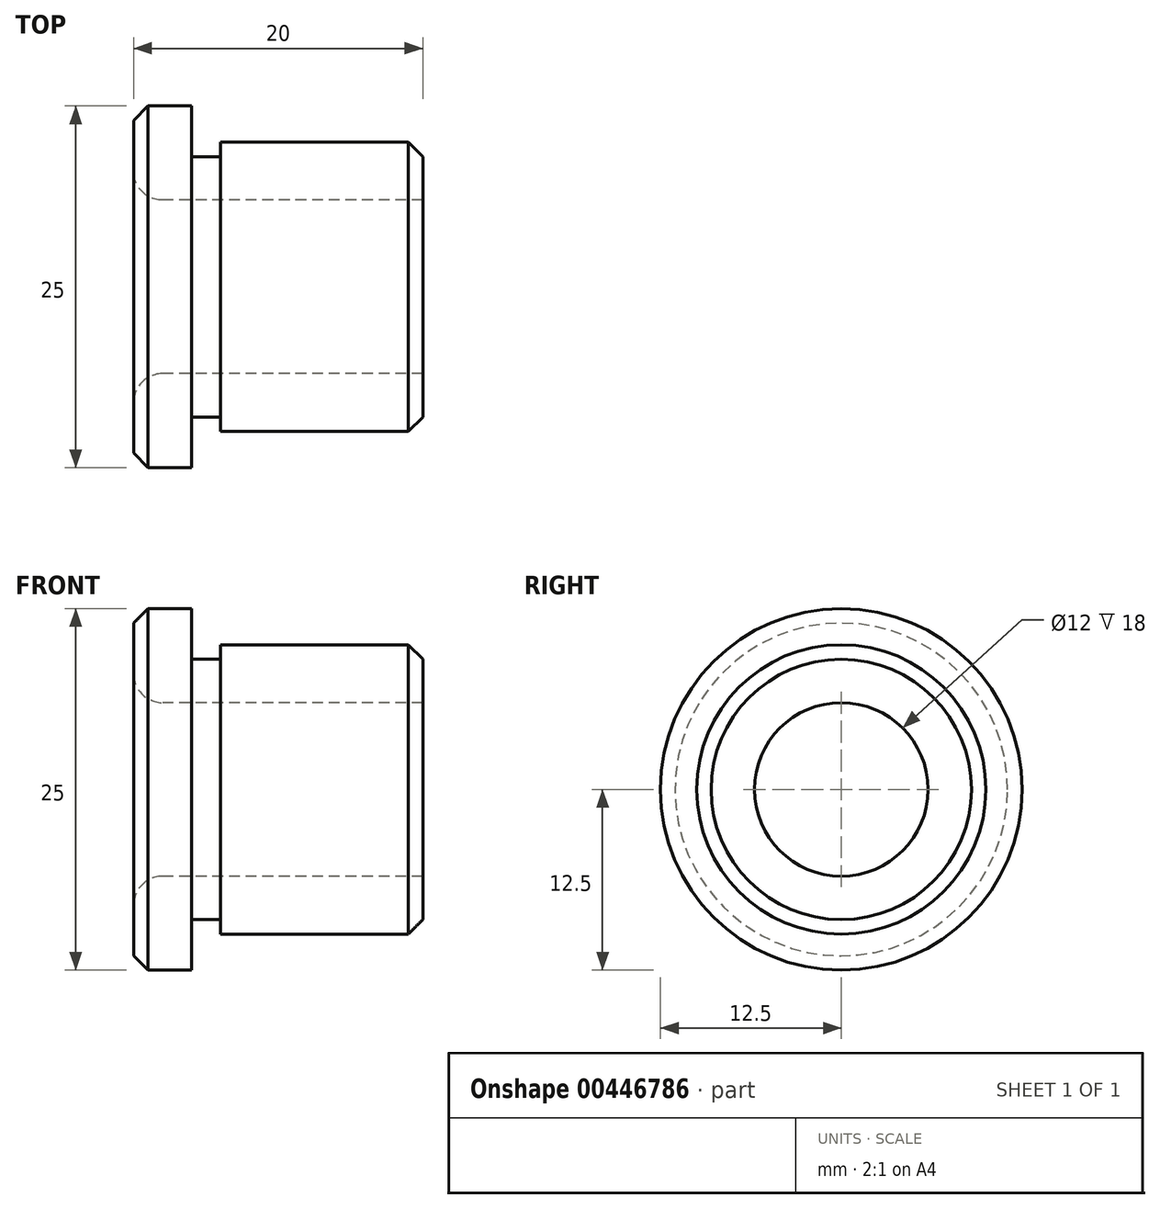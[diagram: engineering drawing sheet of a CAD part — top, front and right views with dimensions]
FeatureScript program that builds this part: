
annotation { "Feature Type Name" : "Feature", "Feature Type Description" : "" }
export const myFeature = defineFeature(function(context is Context, id is Id, definition is map)
    precondition{}
    {
        {
            var Q0;
            Q0=qCreatedBy(makeId("Front.planeOp"),FACE);
            var sketch = newSketch(context, id + "F0", { "sketchPlane" : qUnion([Q0])});
            skLineSegment(sketch, "E0", {"start": v(0, 0) * mm, "end": v(25.35, 0) * mm, "construction": true});
            skLineSegment(sketch, "E1", {"start": v(0, 8) * mm, "end": v(0, 12.5) * mm});
            skLineSegment(sketch, "E2", {"start": v(0, 12.5) * mm, "end": v(4, 12.5) * mm});
            skLineSegment(sketch, "E3", {"start": v(4, 12.5) * mm, "end": v(4, 9) * mm});
            skLineSegment(sketch, "E4", {"start": v(4, 9) * mm, "end": v(6, 9) * mm});
            skLineSegment(sketch, "E5", {"start": v(6, 9) * mm, "end": v(6, 10) * mm});
            skLineSegment(sketch, "E6", {"start": v(6, 10) * mm, "end": v(20, 10) * mm});
            skLineSegment(sketch, "E7", {"start": v(20, 10) * mm, "end": v(20, 6) * mm});
            skLineSegment(sketch, "E8", {"start": v(20, 6) * mm, "end": v(2, 6) * mm});
            skPoint(sketch, "E9.visualSharp", {"position": v(0, 6) * mm});
            skArc(sketch, "E9.filletArc", {"start": v(0, 8) * mm, "mid": v(0.59, 6.59) * mm, "end": v(2, 6) * mm});
            skSolve(sketch);
        }
        {
            var Q0;
            Q0 = qSketchRegion(id + "F0", true);
            var Q1;
            Q1=sQuery(id+"F0.wireOp",EDGE,"E0");
            revolve(context, id + "F1", {"entities" : qUnion([Q0]), "axis" : qUnion([Q1]), "revolveType" : RevolveType.FULL});
        }
        {
            var Q0;
            Q0=makeQuery(id+"F1.opRevolve","SWEPT_EDGE",EDGE,{"disambiguationData":[OSD([sQuery(id+"F0.wireOp",EDGE,"E1"),sQuery(id+"F0.wireOp",EDGE,"E2")])]});
            var Q1;
            Q1=makeQuery(id+"F1.opRevolve","SWEPT_EDGE",EDGE,{"disambiguationData":[OSD([sQuery(id+"F0.wireOp",EDGE,"E6"),sQuery(id+"F0.wireOp",EDGE,"E7")])]});
            chamfer(context, id + "F2", {"entities" : qUnion([Q0, Q1]), "width" : 1 * mm, "tangentPropagation" : true});
        }
    });
